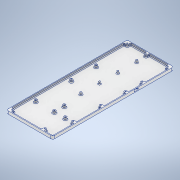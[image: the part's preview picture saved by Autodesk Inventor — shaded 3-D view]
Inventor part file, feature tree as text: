
AUTODESK INVENTOR PART (.ipt)
format: ipt  version: 2022 (Build 260153000, 153)  size: 565,760 bytes
history: native  units: mm
features: sketch x24, hole x15, extrude x7, fillet x4, other x2
ambient origin geometry x8: Origin, YZ Plane, XZ Plane, XY Plane, X Axis, Y Axis, Z Axis, Center Point
bodies: Body1 (feature_tree)
feature tree (52):
  other  "作業平面5"
  extrude  "押し出し12"  Depth=142.24mm
  extrude  "押し出し13"  Depth=371.475mm
  extrude  "押し出し14"  Depth=6.0mm
  extrude  "押し出し15"  Depth=2.6mm TaperAngle=0.0deg
  extrude  "押し出し16"  Depth=6.0mm
  fillet  "フィレット8"  Radius=2.54mm
  sketch  "スケッチ23"
  extrude  "押し出し17"  Depth=6.4mm TaperAngle=0.0deg
  sketch  "スケッチ28"
  sketch  "スケッチ32"
  sketch  "スケッチ33"
  sketch  "スケッチ34"
  sketch  "スケッチ35"
  sketch  "スケッチ36"
  sketch  "スケッチ37"
  sketch  "スケッチ38"
  sketch  "スケッチ39"
  sketch  "スケッチ40"
  sketch  "スケッチ41"
  sketch  "スケッチ42"
  sketch  "スケッチ43"
  sketch  "スケッチ44"
  sketch  "スケッチ45"
  sketch  "スケッチ46"
  sketch  "スケッチ47"
  hole  "穴1"  [1 undecoded]
  hole  "穴2"  [1 undecoded]
  hole  "穴3"  [1 undecoded]
  hole  "穴4"  [1 undecoded]
  hole  "穴5"  [1 undecoded]
  hole  "穴6"  [1 undecoded]
  hole  "穴7"  [1 undecoded]
  hole  "穴8"  [1 undecoded]
  hole  "穴9"  [1 undecoded]
  hole  "穴10"  [1 undecoded]
  hole  "穴11"  [1 undecoded]
  hole  "穴12"  [1 undecoded]
  hole  "穴13"  [1 undecoded]
  hole  "穴14"  [1 undecoded]
  hole  "穴15"  [1 undecoded]
  fillet  "フィレット13"  Radius=56.39mm
  fillet  "フィレット14"  Radius=57.4mm
  extrude  "押し出し18"  Depth=6.4mm TaperAngle=0.0deg
  fillet  "フィレット15"  Radius=2.0mm
  sketch  "スケッチ16"
  other  "ソリッド2"
  sketch  "スケッチ17"
  sketch  "スケッチ18"
  sketch  "スケッチ21"
  sketch  "スケッチ24"
  sketch  "スケッチ48"
note: 15 required parameter values undecoded (feature->parameter linkage not recoverable at this tier; creation-order binding heuristic only, values carry confidence <= 0.55)
